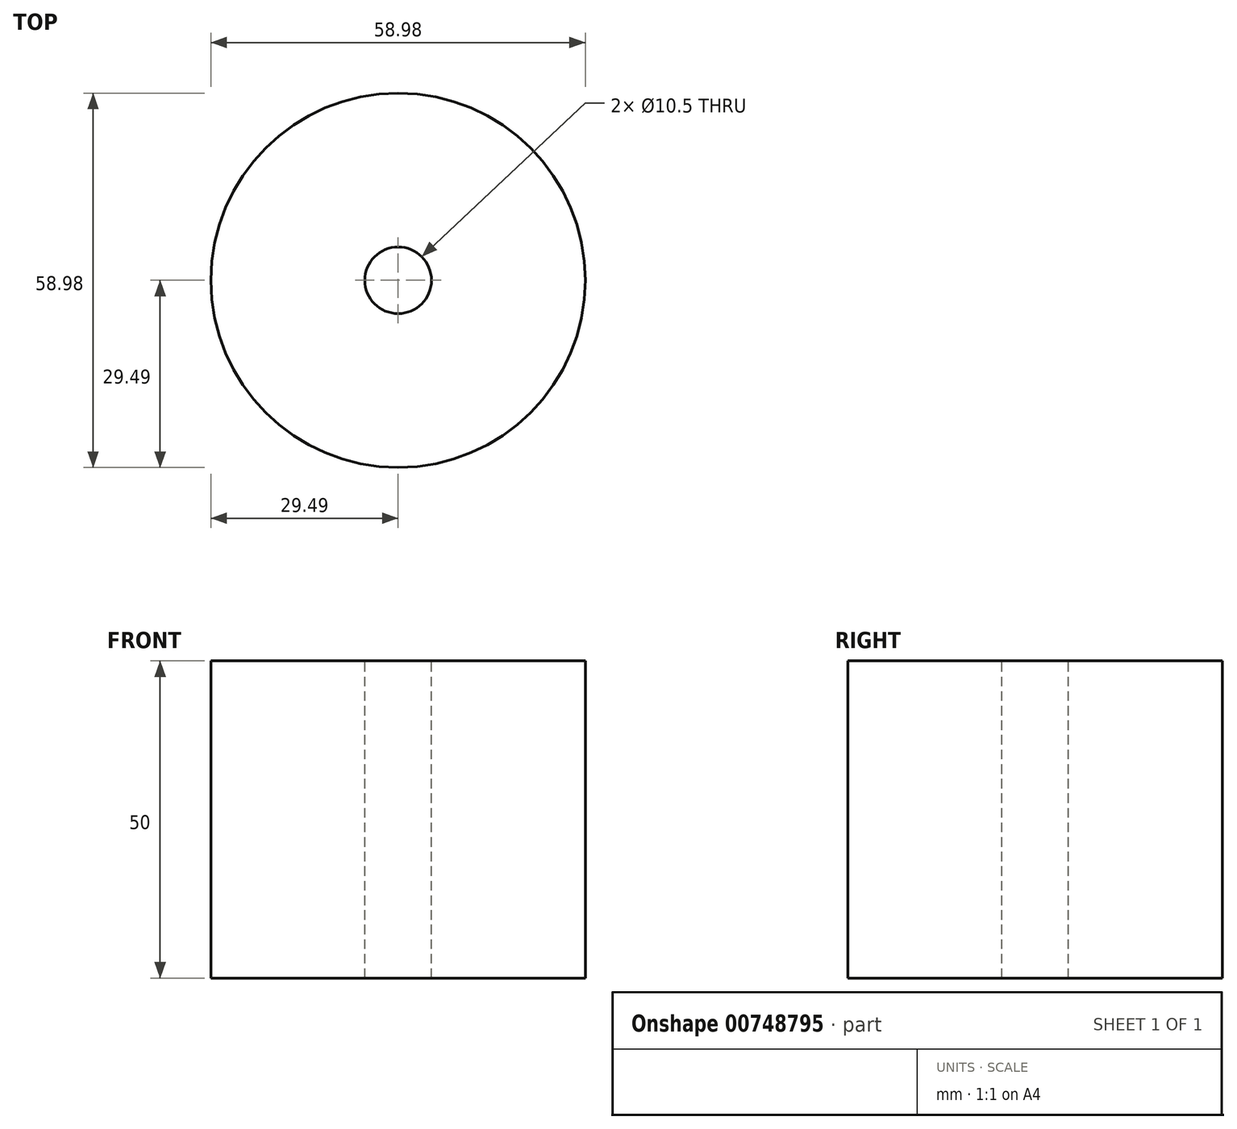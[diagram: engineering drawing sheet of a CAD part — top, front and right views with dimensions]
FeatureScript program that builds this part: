
annotation { "Feature Type Name" : "Feature", "Feature Type Description" : "" }
export const myFeature = defineFeature(function(context is Context, id is Id, definition is map)
    precondition{}
    {
        {
            var Q0;
            Q0=qCreatedBy(makeId("Top.planeOp"),FACE);
            var sketch = newSketch(context, id + "F0", { "sketchPlane" : qUnion([Q0])});
            skCircle(sketch, "E0", {"center": v(0, 0) * mm, "radius": 29.5 * mm});
            skSolve(sketch);
        }
        {
            var Q0;
            Q0=makeQuery(id+"F0.imprint","IMPRINT",FACE,{"disambiguationData":[TD([[makeQuery(id+"F0.imprint","IMPRINT",EDGE,{"derivedFrom":sQuery(id+"F0.wireOp",EDGE,"E0")}),1.0]])]});
            extrude(context, id + "F1", {"entities" : qUnion([Q0]), "depth" : 50 * mm, "offsetDistance" : 25 * mm});
        }
        {
            var Q0;
            Q0=makeQuery(id+"F1.opExtrude","CAP_FACE",FACE,{"disambiguationData":[OSD([sQuery(id+"F0.wireOp",EDGE,"E0")])],"isStart":false});
            var sketch = newSketch(context, id + "F2", { "sketchPlane" : qUnion([Q0])});
            skPoint(sketch, "E1", {"position": v(0, 0) * mm});
            skSolve(sketch);
        }
        {
            var Q0;
            Q0=sQuery(id+"F2.wireOp",VERTEX,"E1");
            var Q1;
            Q1=makeQuery(id+"F1.opExtrude","SWEPT_BODY",BODY,{"disambiguationData":[OSD([sQuery(id+"F0.wireOp",EDGE,"E0")])]});
            hole(context, id + "F3", {"style" : HoleStyle.SIMPLE, "endStyle" : HoleEndStyle.THROUGH, "standardTappedOrClearance" : lookupTablePath({ "standard" : "ISO", "engagement" : "75%", "pitch" : "1.5 mm", "size" : "M12", "type" : "Tapped" }), "standardBlindInLast" : lookupTablePath({ "standard" : "ISO", "engagement" : "75%", "pitch" : "1.5 mm", "size" : "M12", "type" : "Tapped" }), "holeDiameter" : 10.5 * mm, "majorDiameter" : 12 * mm, "showTappedDepth" : true, "isTappedThrough" : true, "tappedDepth" : 12 * mm, "tapClearance" : 3, "locations" : qUnion([Q0]), "scope" : qUnion([Q1])});
        }
    });
